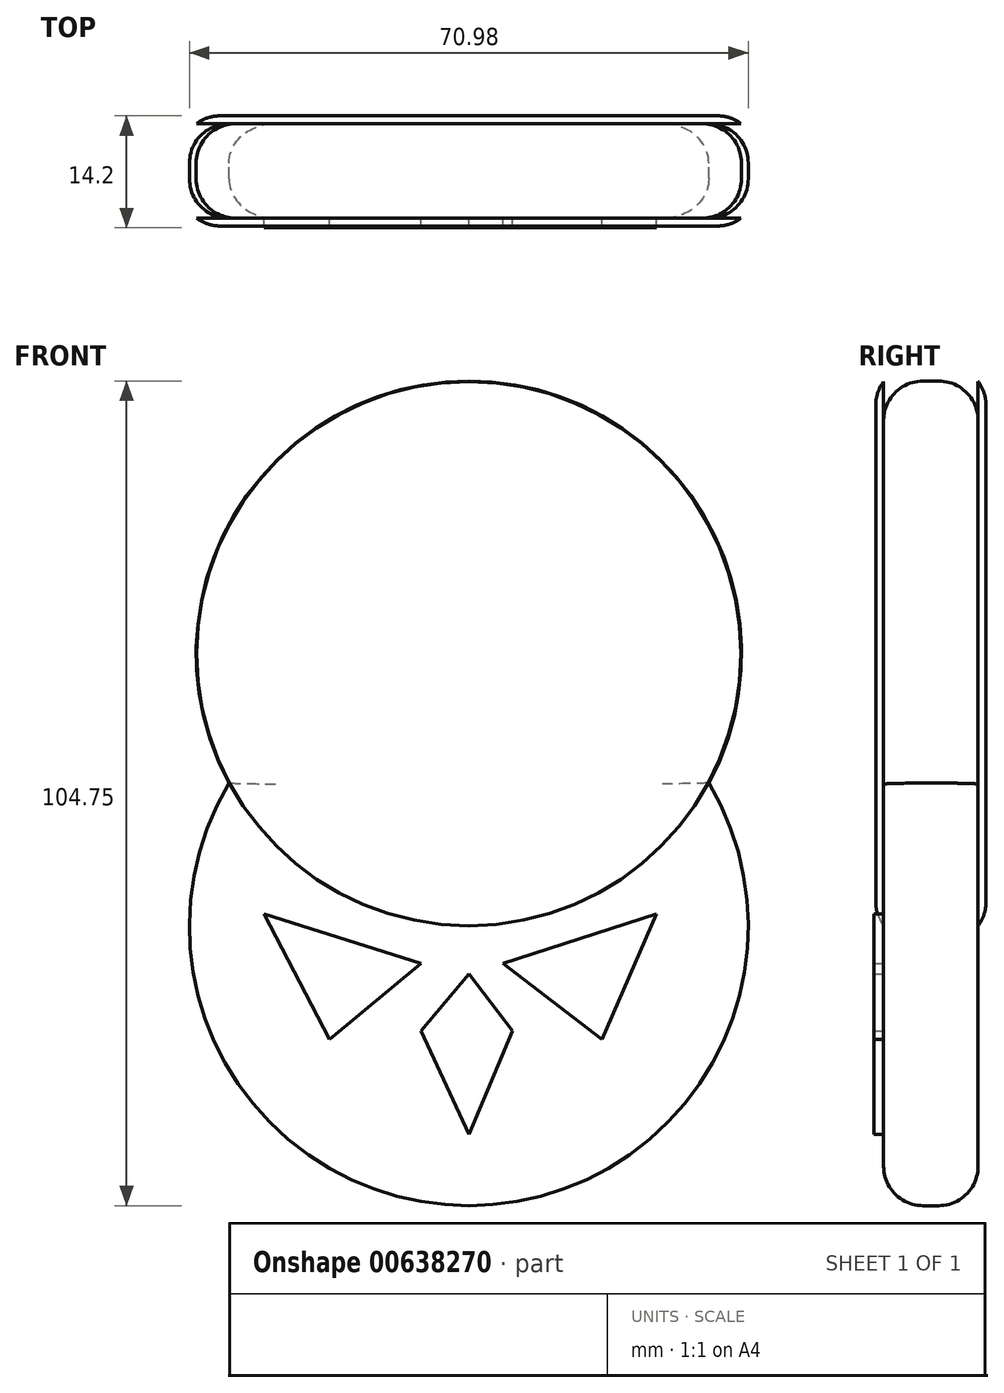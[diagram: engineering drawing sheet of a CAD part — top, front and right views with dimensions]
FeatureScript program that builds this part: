
annotation { "Feature Type Name" : "Feature", "Feature Type Description" : "" }
export const myFeature = defineFeature(function(context is Context, id is Id, definition is map)
    precondition{}
    {
        {
            var Q0;
            Q0=qCreatedBy(makeId("Front.planeOp"),FACE);
            var sketch = newSketch(context, id + "F0", { "sketchPlane" : qUnion([Q0])});
            skCircle(sketch, "E0", {"center": v(0, 26.4) * mm, "radius": 34.63 * mm});
            skCircle(sketch, "E1", {"center": v(0, -8.23) * mm, "radius": 35.49 * mm});
            skSolve(sketch);
        }
        {
            var Q0;
            {var subQ0=sQuery(id+"F0.wireOp",EDGE,"E1");var subQ1=sQuery(id+"F0.wireOp",EDGE,"E0");var subQ2=makeQuery(id+"F0.imprint","INTERSECT",VERTEX,{"disambiguationData":[OD(0.0)],"derivedFrom":[subQ1,subQ0]});Q0=makeQuery(id+"F0.imprint","IMPRINT",FACE,{"disambiguationData":[TD([[makeQuery(id+"F0.imprint","IMPRINT",EDGE,{"disambiguationData":[TD([[subQ2,-1.0]])],"derivedFrom":subQ1}),1.0]])]});}
            var sketch = newSketch(context, id + "F1", { "sketchPlane" : qUnion([Q0])});
            skSolve(sketch);
        }
        {
            var Q0;
            Q0 = qSketchRegion(id + "F1", true);
            var Q1;
            {var subQ0=sQuery(id+"F0.wireOp",EDGE,"E1");var subQ1=sQuery(id+"F0.wireOp",EDGE,"E0");var subQ2=makeQuery(id+"F0.imprint","INTERSECT",VERTEX,{"disambiguationData":[OD(0.0)],"derivedFrom":[subQ1,subQ0]});Q1=makeQuery(id+"F0.imprint","IMPRINT",FACE,{"disambiguationData":[TD([[makeQuery(id+"F0.imprint","IMPRINT",EDGE,{"disambiguationData":[TD([[subQ2,1.0]])],"derivedFrom":subQ1}),1.0]])]});}
            var Q2;
            {var subQ0=sQuery(id+"F0.wireOp",EDGE,"E1");var subQ1=sQuery(id+"F0.wireOp",EDGE,"E0");var subQ2=makeQuery(id+"F0.imprint","INTERSECT",VERTEX,{"disambiguationData":[OD(0.0)],"derivedFrom":[subQ1,subQ0]});Q2=makeQuery(id+"F0.imprint","IMPRINT",FACE,{"disambiguationData":[TD([[makeQuery(id+"F0.imprint","IMPRINT",EDGE,{"disambiguationData":[TD([[subQ2,-1.0]])],"derivedFrom":subQ1}),1.0]])]});}
            var Q3;
            {var subQ0=sQuery(id+"F0.wireOp",EDGE,"E1");var subQ1=sQuery(id+"F0.wireOp",EDGE,"E0");var subQ2=makeQuery(id+"F0.imprint","INTERSECT",VERTEX,{"disambiguationData":[OD(0.0)],"derivedFrom":[subQ1,subQ0]});Q3=makeQuery(id+"F0.imprint","IMPRINT",FACE,{"disambiguationData":[TD([[makeQuery(id+"F0.imprint","IMPRINT",EDGE,{"disambiguationData":[TD([[subQ2,-1.0]])],"derivedFrom":subQ1}),-1.0]])]});}
            extrude(context, id + "F2", {"entities" : qUnion([Q0, Q1, Q2, Q3]), "depth" : 12 * mm, "offsetDistance" : 25 * mm});
        }
        {
            var Q0;
            Q0=makeQuery(id+"F2.opExtrude","CAP_FACE",FACE,{"disambiguationData":[OSD([sQuery(id+"F0.wireOp",EDGE,"E0"),sQuery(id+"F0.wireOp",EDGE,"E1")])],"isStart":false});
            var sketch = newSketch(context, id + "F3", { "sketchPlane" : qUnion([Q0])});
            skCircle(sketch, "E2", {"center": v(0, 26.4) * mm, "radius": 34.56 * mm});
            skSolve(sketch);
        }
        {
            var Q0;
            Q0 = qSketchRegion(id + "F3", true);
            extrude(context, id + "F4", {"entities" : qUnion([Q0]), "depth" : 1 * mm, "offsetDistance" : 25 * mm});
        }
        {
            var Q0;
            Q0=makeQuery(id+"F2.opExtrude","CAP_FACE",FACE,{"disambiguationData":[OSD([sQuery(id+"F0.wireOp",EDGE,"E0"),sQuery(id+"F0.wireOp",EDGE,"E1")])],"isStart":true});
            var sketch = newSketch(context, id + "F5", { "sketchPlane" : qUnion([Q0])});
            skCircle(sketch, "E3", {"center": v(0, 26.4) * mm, "radius": 34.58 * mm});
            skSolve(sketch);
        }
        {
            var Q0;
            Q0 = qSketchRegion(id + "F5", true);
            extrude(context, id + "F6", {"entities" : qUnion([Q0]), "depth" : 1 * mm, "offsetDistance" : 25 * mm});
        }
        {
            var Q0;
            Q0=makeQuery(id+"F2.opExtrude","CAP_FACE",FACE,{"disambiguationData":[OSD([sQuery(id+"F0.wireOp",EDGE,"E0"),sQuery(id+"F0.wireOp",EDGE,"E1")])],"isStart":false});
            var Q1;
            Q1=makeQuery(id+"F6.opExtrude","CAP_FACE",FACE,{"disambiguationData":[OSD([sQuery(id+"F5.wireOp",EDGE,"E3")])],"isStart":false});
            var Q2;
            Q2=makeQuery(id+"F2.opExtrude","CAP_FACE",FACE,{"disambiguationData":[OSD([sQuery(id+"F0.wireOp",EDGE,"E0"),sQuery(id+"F0.wireOp",EDGE,"E1")])],"isStart":true});
            fillet(context, id + "F7", {"entities" : qUnion([Q0, Q1, Q2]), "radius" : 5 * mm, "tangentPropagation" : true, "allowEdgeOverflow" : false});
        }
        {
            var Q0;
            Q0=makeQuery(id+"F4.opExtrude","CAP_FACE",FACE,{"disambiguationData":[OSD([sQuery(id+"F3.wireOp",EDGE,"E2")])],"isStart":false});
            fillet(context, id + "F8", {"entities" : qUnion([Q0]), "radius" : 5 * mm, "tangentPropagation" : true, "allowEdgeOverflow" : false});
        }
        {
            var Q0;
            Q0=makeQuery(id+"F2.opExtrude","CAP_FACE",FACE,{"disambiguationData":[OSD([sQuery(id+"F0.wireOp",EDGE,"E0"),sQuery(id+"F0.wireOp",EDGE,"E1")])],"isStart":false});
            var sketch = newSketch(context, id + "F9", { "sketchPlane" : qUnion([Q0])});
            skLineSegment(sketch, "E4", {"start": v(-26.04, -6.63) * mm, "end": v(-17.7, -22.63) * mm});
            skLineSegment(sketch, "E5", {"start": v(-17.7, -22.63) * mm, "end": v(-6.08, -12.92) * mm});
            skLineSegment(sketch, "E6", {"start": v(-6.08, -12.92) * mm, "end": v(-26.04, -6.63) * mm});
            skLineSegment(sketch, "E7", {"start": v(4.3, -12.92) * mm, "end": v(23.86, -6.63) * mm});
            skLineSegment(sketch, "E8", {"start": v(23.86, -6.63) * mm, "end": v(16.88, -22.63) * mm});
            skLineSegment(sketch, "E9", {"start": v(16.88, -22.63) * mm, "end": v(4.3, -12.92) * mm});
            skLineSegment(sketch, "E10", {"start": v(0, -14.29) * mm, "end": v(-6.08, -21.53) * mm});
            skLineSegment(sketch, "E11", {"start": v(-6.08, -21.53) * mm, "end": v(0, -34.66) * mm});
            skLineSegment(sketch, "E12", {"start": v(0, -34.66) * mm, "end": v(5.54, -21.53) * mm});
            skLineSegment(sketch, "E13", {"start": v(5.54, -21.53) * mm, "end": v(0, -14.29) * mm});
            skSolve(sketch);
        }
        {
            var Q0;
            Q0 = qSketchRegion(id + "F9", true);
            extrude(context, id + "F10", {"entities" : qUnion([Q0]), "operationType" : NewBodyOperationType.ADD, "depth" : 1.2 * mm, "offsetDistance" : 25 * mm});
        }
    });
